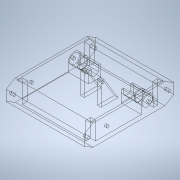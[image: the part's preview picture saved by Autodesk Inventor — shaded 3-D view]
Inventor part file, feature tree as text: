
AUTODESK INVENTOR PART (.ipt)
format: ipt  version: 2020 (Build 240168000, 168)  size: 304,640 bytes
history: native  units: in
note: dims shown in document units (in); Inventor stores cm internally (conversion verified against a paired STEP export)
features: extrude x9, sketch x9, mirror x4, projected_geometry x4, plane x1
ambient origin geometry x8: Origin, YZ Plane, XZ Plane, XY Plane, X Axis, Y Axis, Z Axis, Center Point
bodies: Solid1 (feature_tree)
feature tree (27):
  extrude  "Extrusion1"  Depth=5.9055in
  extrude  "Extrusion2"  TaperAngle=0.0deg  [1 undecoded]
  extrude  "Extrusion3"  Depth=1.2598in
  extrude  "Extrusion4"  Depth=0.315in
  extrude  "Extrusion5"  TaperAngle=0.0deg  [1 undecoded]
  extrude  "Extrusion6"  Depth=0.689in
  mirror  "Mirror1"
  extrude  "Extrusion7"  Depth=0.0787in
  mirror  "Mirror2"
  extrude  "Extrusion8"  Depth=0.5512in
  mirror  "Mirror3"
  plane  "Work Plane1"
  extrude  "Extrusion9"  Depth=0.7874in TaperAngle=0.0deg
  mirror  "Mirror4"
  sketch  "Sketch1"  dims[d0=1.378in d1=5.9055in]
  sketch  "Sketch2"  dims[d2=5.1181in d3=0.0in]
  projected_geometry  "Projected Loop1"
  sketch  "Sketch3"  dims[d4=0.1575in d5=1.2598in]
  projected_geometry  "Projected Loop2"
  projected_geometry  "Projected Loop3"
  sketch  "Sketch4"  dims[d6=0.0in d8=0.315in]
  sketch  "Sketch5"  dims[d10=1.1898in d11=0.0in]
  projected_geometry  "Projected Loop4"
  sketch  "Sketch6"  dims[d12=0.6496in d13=0.689in]
  sketch  "Sketch7"  dims[d14=1.5748in d15=0.0787in]
  sketch  "Sketch9"  dims[d16=0.5512in d17=0.0in d18=0.6102in]
  sketch  "Sketch10"  dims[d19=0.4803in d20=0.7874in d21=0.0in d22=0.1654in d23=6.063in d24=0.0in d25=0.5967in d26=0.1575in d27=1.5748in d28=0.0in d29=0.0in d30=0.1575in d31=0.2756in d32=0.0in d33=0.4331in d34=0.122in d35=0.0787in d36=0.0787in d37=0.0787in d38=2.7559in d39=0.122in d40=0.061in d41=0.0787in d42=0.2362in d43=0.0in]
note: 2 required parameter values undecoded (feature->parameter linkage not recoverable at this tier; creation-order binding heuristic only, values carry confidence <= 0.55)
